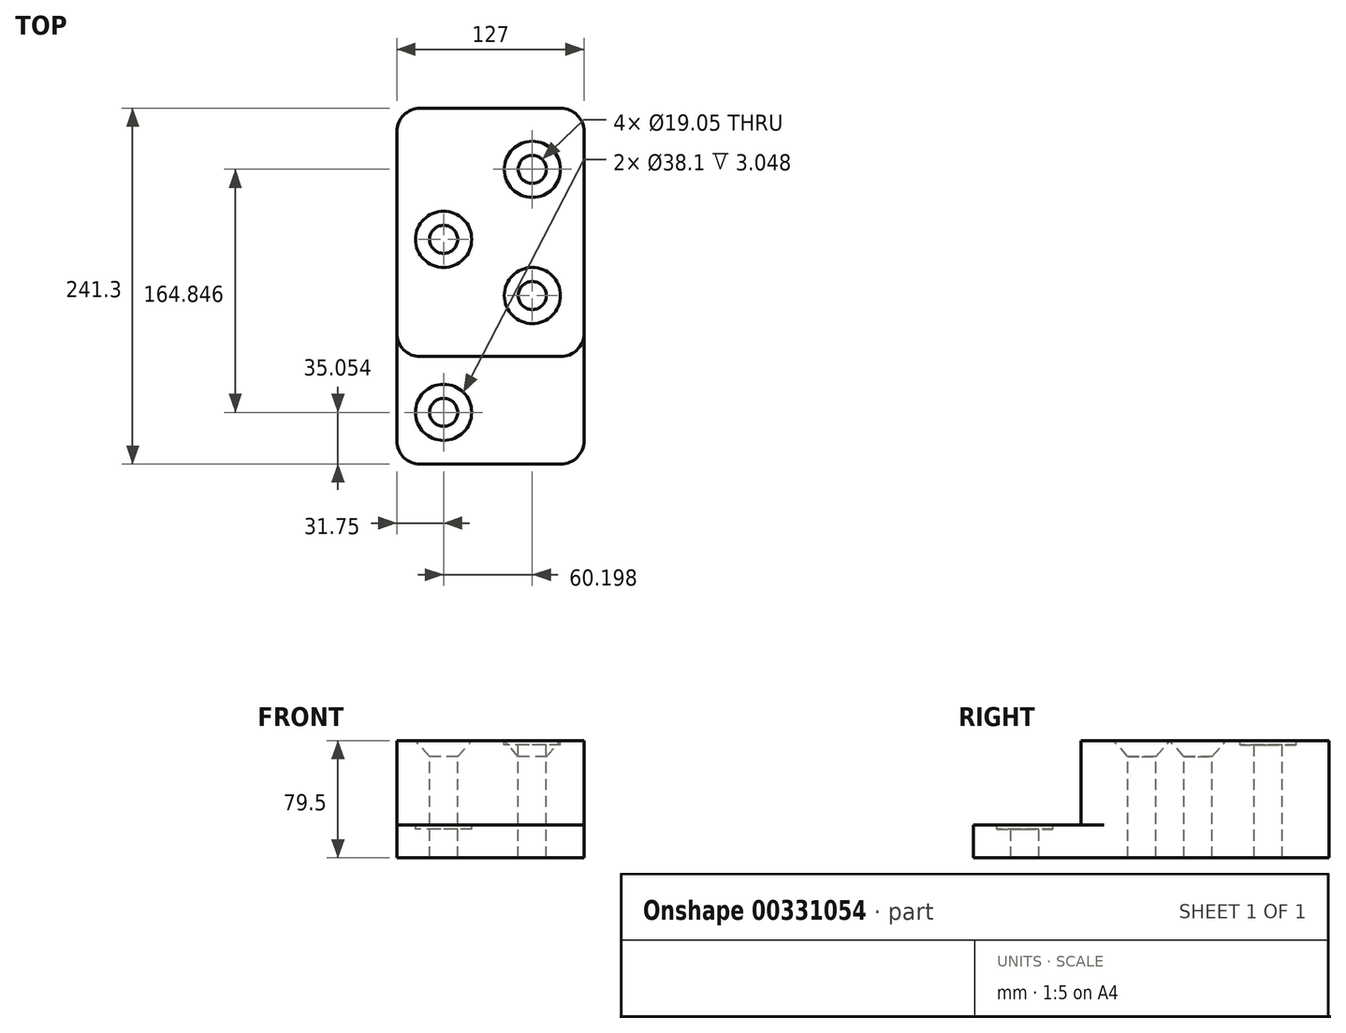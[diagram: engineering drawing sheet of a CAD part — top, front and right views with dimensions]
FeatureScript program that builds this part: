
annotation { "Feature Type Name" : "Feature", "Feature Type Description" : "" }
export const myFeature = defineFeature(function(context is Context, id is Id, definition is map)
    precondition{}
    {
        {
            var Q0;
            Q0=qCreatedBy(makeId("Top.planeOp"),FACE);
            var sketch = newSketch(context, id + "F0", { "sketchPlane" : qUnion([Q0])});
            skLineSegment(sketch, "E0.bottom", {"start": v(-63.5, 168.4) * mm, "end": v(63.5, 168.4) * mm});
            skLineSegment(sketch, "E0.top", {"start": v(-63.5, 0) * mm, "end": v(63.5, 0) * mm});
            skLineSegment(sketch, "E0.left", {"start": v(-63.5, 168.4) * mm, "end": v(-63.5, 0) * mm});
            skLineSegment(sketch, "E0.right", {"start": v(63.5, 168.4) * mm, "end": v(63.5, 0) * mm});
            skLineSegment(sketch, "E1.top", {"start": v(-63.5, -72.9) * mm, "end": v(63.5, -72.9) * mm});
            skLineSegment(sketch, "E1.left", {"start": v(-63.5, 0) * mm, "end": v(-63.5, -72.9) * mm});
            skLineSegment(sketch, "E1.right", {"start": v(63.5, 0) * mm, "end": v(63.5, -72.9) * mm});
            skSolve(sketch);
        }
        {
            var Q0;
            Q0=makeQuery(id+"F0.imprint","IMPRINT",FACE,{"disambiguationData":[TD([[makeQuery(id+"F0.imprint","IMPRINT",EDGE,{"derivedFrom":sQuery(id+"F0.wireOp",EDGE,"E0.bottom")}),-1.0]])]});
            extrude(context, id + "F1", {"entities" : qUnion([Q0]), "depth" : 79.5 * mm});
        }
        {
            var Q0;
            Q0=makeQuery(id+"F0.imprint","IMPRINT",FACE,{"disambiguationData":[TD([[makeQuery(id+"F0.imprint","IMPRINT",EDGE,{"derivedFrom":sQuery(id+"F0.wireOp",EDGE,"E0.top")}),-1.0]])]});
            extrude(context, id + "F2", {"entities" : qUnion([Q0]), "operationType" : NewBodyOperationType.ADD, "depth" : 22.35 * mm});
        }
        {
            var Q0;
            Q0=makeQuery(id+"F1.opExtrude","SWEPT_EDGE",EDGE,{"disambiguationData":[OSD([sQuery(id+"F0.wireOp",EDGE,"E0.right"),sQuery(id+"F0.wireOp",EDGE,"E0.top"),sQuery(id+"F0.wireOp",EDGE,"E1.right")])]});
            var Q1;
            Q1=makeQuery(id+"F1.opExtrude","SWEPT_EDGE",EDGE,{"disambiguationData":[OSD([sQuery(id+"F0.wireOp",EDGE,"E0.left"),sQuery(id+"F0.wireOp",EDGE,"E0.top"),sQuery(id+"F0.wireOp",EDGE,"E1.left")])]});
            var Q2;
            Q2=makeQuery(id+"F2.opExtrude","SWEPT_EDGE",EDGE,{"disambiguationData":[OSD([sQuery(id+"F0.wireOp",EDGE,"E1.top"),sQuery(id+"F0.wireOp",EDGE,"E1.right")])]});
            var Q3;
            Q3=makeQuery(id+"F2.opExtrude","SWEPT_EDGE",EDGE,{"disambiguationData":[OSD([sQuery(id+"F0.wireOp",EDGE,"E1.top"),sQuery(id+"F0.wireOp",EDGE,"E1.left")])]});
            var Q4;
            Q4=makeQuery(id+"F1.opExtrude","SWEPT_EDGE",EDGE,{"disambiguationData":[OSD([sQuery(id+"F0.wireOp",EDGE,"E0.bottom"),sQuery(id+"F0.wireOp",EDGE,"E0.right")])]});
            var Q5;
            Q5=makeQuery(id+"F1.opExtrude","SWEPT_EDGE",EDGE,{"disambiguationData":[OSD([sQuery(id+"F0.wireOp",EDGE,"E0.bottom"),sQuery(id+"F0.wireOp",EDGE,"E0.left")])]});
            fillet(context, id + "F3", {"entities" : qUnion([Q0, Q1, Q2, Q3, Q4, Q5]), "radius" : 15.75 * mm, "tangentPropagation" : true, "allowEdgeOverflow" : false});
        }
        {
            var Q0;
            Q0=makeQuery(id+"F1.opExtrude","CAP_FACE",FACE,{"disambiguationData":[OSD([sQuery(id+"F0.wireOp",EDGE,"E0.bottom"),sQuery(id+"F0.wireOp",EDGE,"E0.left"),sQuery(id+"F0.wireOp",EDGE,"E0.right"),sQuery(id+"F0.wireOp",EDGE,"E0.top")])],"isStart":false});
            var sketch = newSketch(context, id + "F4", { "sketchPlane" : qUnion([Q0])});
            skPoint(sketch, "E2", {"position": v(-31.75, 79.5) * mm});
            skPoint(sketch, "E3", {"position": v(28.45, 41.4) * mm});
            skPoint(sketch, "E4", {"position": v(28.45, 127) * mm});
            skSolve(sketch);
        }
        {
            var Q0;
            Q0=sQuery(id+"F4.wireOp",VERTEX,"E2");
            var Q1;
            Q1=sQuery(id+"F4.wireOp",VERTEX,"E3");
            var Q2;
            Q2=makeQuery(id+"F1.opExtrude","SWEPT_BODY",BODY,{"disambiguationData":[OSD([sQuery(id+"F0.wireOp",EDGE,"E0.bottom"),sQuery(id+"F0.wireOp",EDGE,"E0.left"),sQuery(id+"F0.wireOp",EDGE,"E0.right"),sQuery(id+"F0.wireOp",EDGE,"E0.top")])]});
            hole(context, id + "F5", {"style" : HoleStyle.C_SINK, "endStyle" : HoleEndStyle.THROUGH, "holeDiameter" : 19.05 * mm, "cSinkDiameter" : 38.1 * mm, "cSinkAngle" : 82 * degree, "tappedDepth" : 12.7 * mm, "tapClearance" : 3, "locations" : qUnion([Q0, Q1]), "scope" : qUnion([Q2])});
        }
        {
            var Q0;
            Q0=sQuery(id+"F4.wireOp",VERTEX,"E4");
            var Q1;
            Q1=makeQuery(id+"F1.opExtrude","SWEPT_BODY",BODY,{"disambiguationData":[OSD([sQuery(id+"F0.wireOp",EDGE,"E0.bottom"),sQuery(id+"F0.wireOp",EDGE,"E0.left"),sQuery(id+"F0.wireOp",EDGE,"E0.right"),sQuery(id+"F0.wireOp",EDGE,"E0.top")])]});
            hole(context, id + "F6", {"style" : HoleStyle.C_BORE, "endStyle" : HoleEndStyle.THROUGH, "holeDiameter" : 19.05 * mm, "cBoreDiameter" : 38.1 * mm, "cBoreDepth" : 3.05 * mm, "tappedDepth" : 12.7 * mm, "tapClearance" : 3, "locations" : qUnion([Q0]), "scope" : qUnion([Q1])});
        }
        {
            var Q0;
            Q0=makeQuery(id+"F2.opExtrude","CAP_FACE",FACE,{"disambiguationData":[OSD([sQuery(id+"F0.wireOp",EDGE,"E0.top"),sQuery(id+"F0.wireOp",EDGE,"E1.top"),sQuery(id+"F0.wireOp",EDGE,"E1.left"),sQuery(id+"F0.wireOp",EDGE,"E1.right")])],"isStart":false});
            var sketch = newSketch(context, id + "F7", { "sketchPlane" : qUnion([Q0])});
            skPoint(sketch, "E5", {"position": v(-31.75, -37.85) * mm});
            skSolve(sketch);
        }
        {
            var Q0;
            Q0=sQuery(id+"F7.wireOp",VERTEX,"E5");
            var Q1;
            Q1=makeQuery(id+"F1.opExtrude","SWEPT_BODY",BODY,{"disambiguationData":[OSD([sQuery(id+"F0.wireOp",EDGE,"E0.bottom"),sQuery(id+"F0.wireOp",EDGE,"E0.left"),sQuery(id+"F0.wireOp",EDGE,"E0.right"),sQuery(id+"F0.wireOp",EDGE,"E0.top")])]});
            hole(context, id + "F8", {"style" : HoleStyle.C_BORE, "endStyle" : HoleEndStyle.THROUGH, "holeDiameter" : 19.05 * mm, "cBoreDiameter" : 38.1 * mm, "cBoreDepth" : 3.05 * mm, "tappedDepth" : 12.7 * mm, "tapClearance" : 3, "locations" : qUnion([Q0]), "scope" : qUnion([Q1])});
        }
    });
